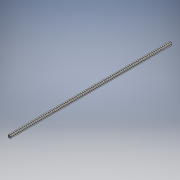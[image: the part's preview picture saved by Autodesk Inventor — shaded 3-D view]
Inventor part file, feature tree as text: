
AUTODESK INVENTOR PART (.ipt)
format: ipt  version: 2018 (Build 220112000, 112)  size: 154,624 bytes
history: native  units: mm
features: extrude x1, sketch x1
ambient origin geometry x8: Origin, YZ Plane, XZ Plane, XY Plane, X Axis, Y Axis, Z Axis, Center Point
bodies: Volumenkörper1 (feature_tree)
feature tree (2):
  extrude  "Extrusion1"  Depth=3.0mm
  sketch  "Skizze1"  dims[d0=3.0mm d1=3.0mm d2=0.5mm d3=1.0mm d4=1.0mm d5=1.2mm d6=1.2mm d7=1.2mm d8=1.2mm d9=0.3mm d10=0.15mm d11=0.15mm d12=0.15mm d13=0.15mm d14=200.0mm d15=0.0mm]
